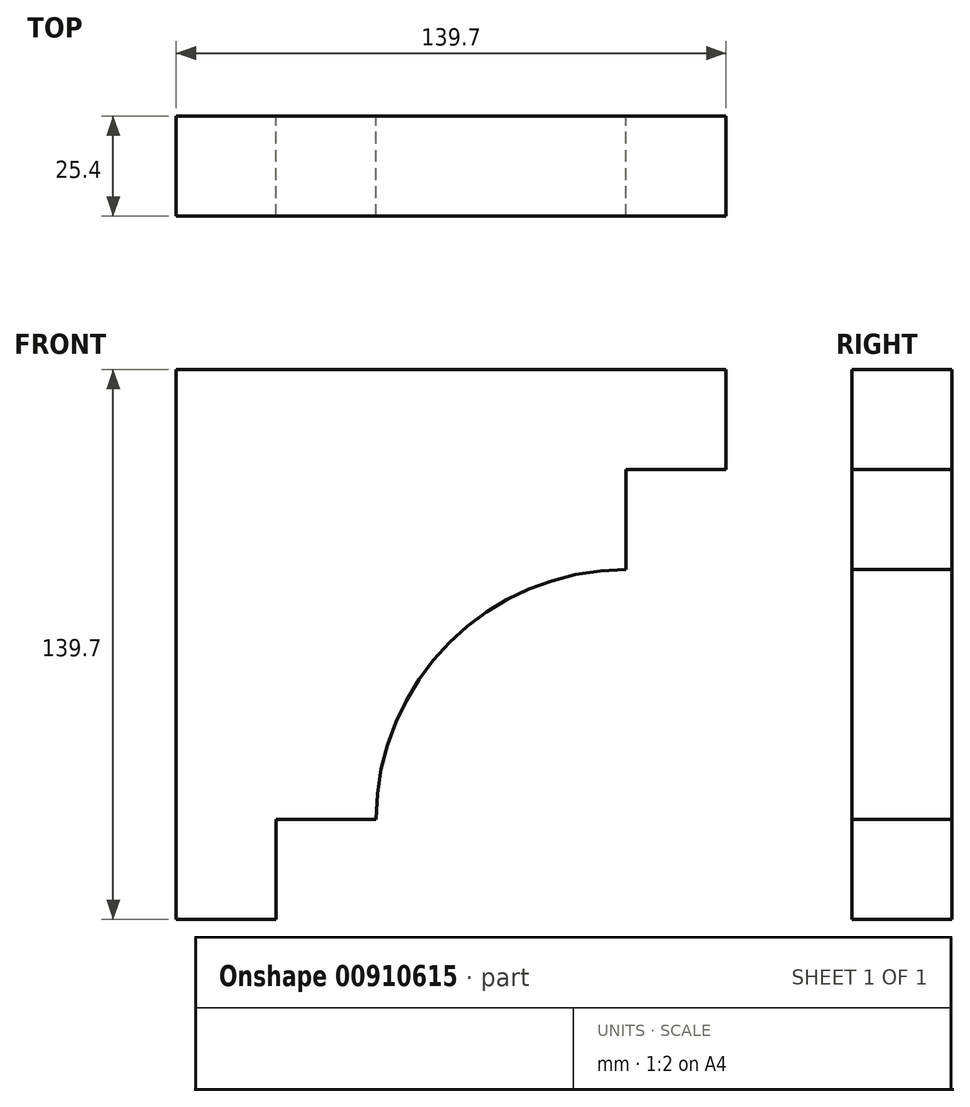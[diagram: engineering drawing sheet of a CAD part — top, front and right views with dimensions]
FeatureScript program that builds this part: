
annotation { "Feature Type Name" : "Feature", "Feature Type Description" : "" }
export const myFeature = defineFeature(function(context is Context, id is Id, definition is map)
    precondition{}
    {
        {
            var Q0;
            Q0=qCreatedBy(makeId("Front.planeOp"),FACE);
            var sketch = newSketch(context, id + "F0", { "sketchPlane" : qUnion([Q0])});
            skLineSegment(sketch, "E0", {"start": v(0, 0) * mm, "end": v(139.7, 0) * mm});
            skLineSegment(sketch, "E1", {"start": v(139.7, 0) * mm, "end": v(139.7, -25.4) * mm});
            skLineSegment(sketch, "E2", {"start": v(139.7, -25.4) * mm, "end": v(114.3, -25.4) * mm});
            skLineSegment(sketch, "E3", {"start": v(0, 0) * mm, "end": v(0, -139.7) * mm});
            skLineSegment(sketch, "E4", {"start": v(0, -139.7) * mm, "end": v(25.4, -139.7) * mm});
            skLineSegment(sketch, "E5", {"start": v(25.4, -139.7) * mm, "end": v(25.4, -114.3) * mm});
            skLineSegment(sketch, "E6", {"start": v(25.4, -114.3) * mm, "end": v(50.8, -114.3) * mm});
            skLineSegment(sketch, "E7", {"start": v(114.3, -25.4) * mm, "end": v(114.3, -50.8) * mm});
            skArc(sketch, "E8", {"start": v(114.3, -50.8) * mm, "mid": v(69.4, -69.4) * mm, "end": v(50.8, -114.3) * mm});
            skLineSegment(sketch, "E9", {"start": v(114.3, -50.8) * mm, "end": v(125.3, -50.8) * mm, "construction": true});
            skLineSegment(sketch, "E10", {"start": v(50.8, -114.3) * mm, "end": v(50.8, -135.78) * mm, "construction": true});
            skSolve(sketch);
        }
        {
            var Q0;
            Q0 = qSketchRegion(id + "F0", true);
            extrude(context, id + "F1", {"entities" : qUnion([Q0]), "depth" : 25.4 * mm, "offsetDistance" : 25.4 * mm});
        }
    });
